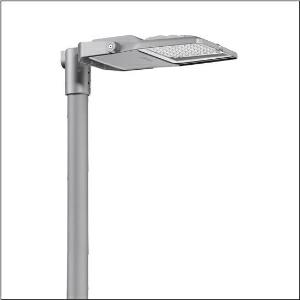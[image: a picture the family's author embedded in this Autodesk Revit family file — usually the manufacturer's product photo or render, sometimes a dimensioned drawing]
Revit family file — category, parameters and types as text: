
# Revit family: floodlight_fl_21_iq_mini___pl52_5xa7771b4d3a_0091
name_source: partatom
category: Lighting Fixtures
units: mm (PartAtom-declared; Revit-internal decimal feet)

## family parameters
Cut with Voids When Loaded = No
Host = Face
Light Source = No
Part Type = Normal
Room Calculation Point = No
Round Connector Dimension = Use Diameter
Shared = No

## types (1)
- --- (1 x LED, 6490 lm, 45.5 W, 4000K)
    Apparent Load = 46 VA
    CIE Flux Codes = 26 60 98 100 100
    Color Rendering = 70
    Color Temperature = 4000K
    Default Elevation = 1800 mm
    Description = Floodlight FL 21 iQ mini, floodlight, primary light control with lens, of PMMA, primary optical cover: protective disc, of toughened safety glass, transparent, light distribution: PL52, light emission: direct distribution, installation type: surface-mounted, LED, High Power LED, rated luminous flux: 6.490lm, luminous efficacy: 143lm/W, light colour: 740, colour temperature: 4000K, control: Auto-Match, Temp-Guard, Lumen-Switch, Night-Set, Smart-Wire, Light-Fading, Desk-Remote (wireless, voltage-free reading and setting of iQ features in the workshop via application-optimized NFC function/RFID function), optimised constant luminous flux control (CLO 2.0), with terminal, 6-pole, mains connection: 220..240V, AC, 50/60Hz, start of lifetime: 46W, end of service life: 48W, reduction: 22W, luminaire housing, of diecast aluminium, powder-coated, Siteco® metallic grey (DB 702S), corrosivity category C5 mid according to DIN EN ISO 12944, sealing non-destructively replaceable, please order mast flange separately, mast bracket, of steel, galvanised, powder-coated, Siteco® metallic grey (DB 702S), protection rating (complete): IP66, insulation class (complete): insulation class II (safety insulation), certification: CE, ENEC, VDE, protection symbol: D, impact resistance: IK08, permissible operating ambient temperature: -40..+40°C, permissible operating ambient temperature for outdoor applications: -40..+50°C, standard: DIN EN 12944, LABS conformity tested according to VDMA 24364:2018-05, packaging unit: 1 piece

Light Distribution: PL52
    Height = 70 mm
    Lamp = 1 x LED
    Lamp Light Flux = 6490 lm
    Lamp Power = 45.5 W
    Lamp count = 1
    Length = 485 mm
    Luminous efficacy = 143 lm/W
    Manufacturer = Siteco
    ModVariant = No
    Model = 5XA7771B4D3A
    Number of Poles = 1
    OnlyDefault = Yes
    Power Factor = 1
    Product Name = Floodlight FL 21 iQ mini | PL52
    Product group = floodlight | pylon annexe
    ProductGroupID = 6200
    Protection Class = Protection class II
    Protection Degree = IP 66
    RLX_Detail_Level = 1
    RLX_Emergency_Light_Flux = 0 lm
    RLX_Emergency_Type = 0
    RLX_Emergency_Type_DB = No
    RlxData = <blob elided: 101365 chars, md5=a744a720>
    Socket = socket
    Standby Power = 0 W
    System Light Flux = 6490 lm
    System Power = 46 W
    Type Comments = factory setting: luminous flux: 100 % | dim-lin: 254 | 463 mA
    Type Image = l_1007125.jpg
    URL = http://relux.com
    VarID = @adj_135321
    Voltage = 0 V
    Weight = 0.00 kg
    Width = 337 mm

## geometry (parser evidence)
native form markers: Blend x4, Sweep x13
no freeform markers — native parametric forms only
